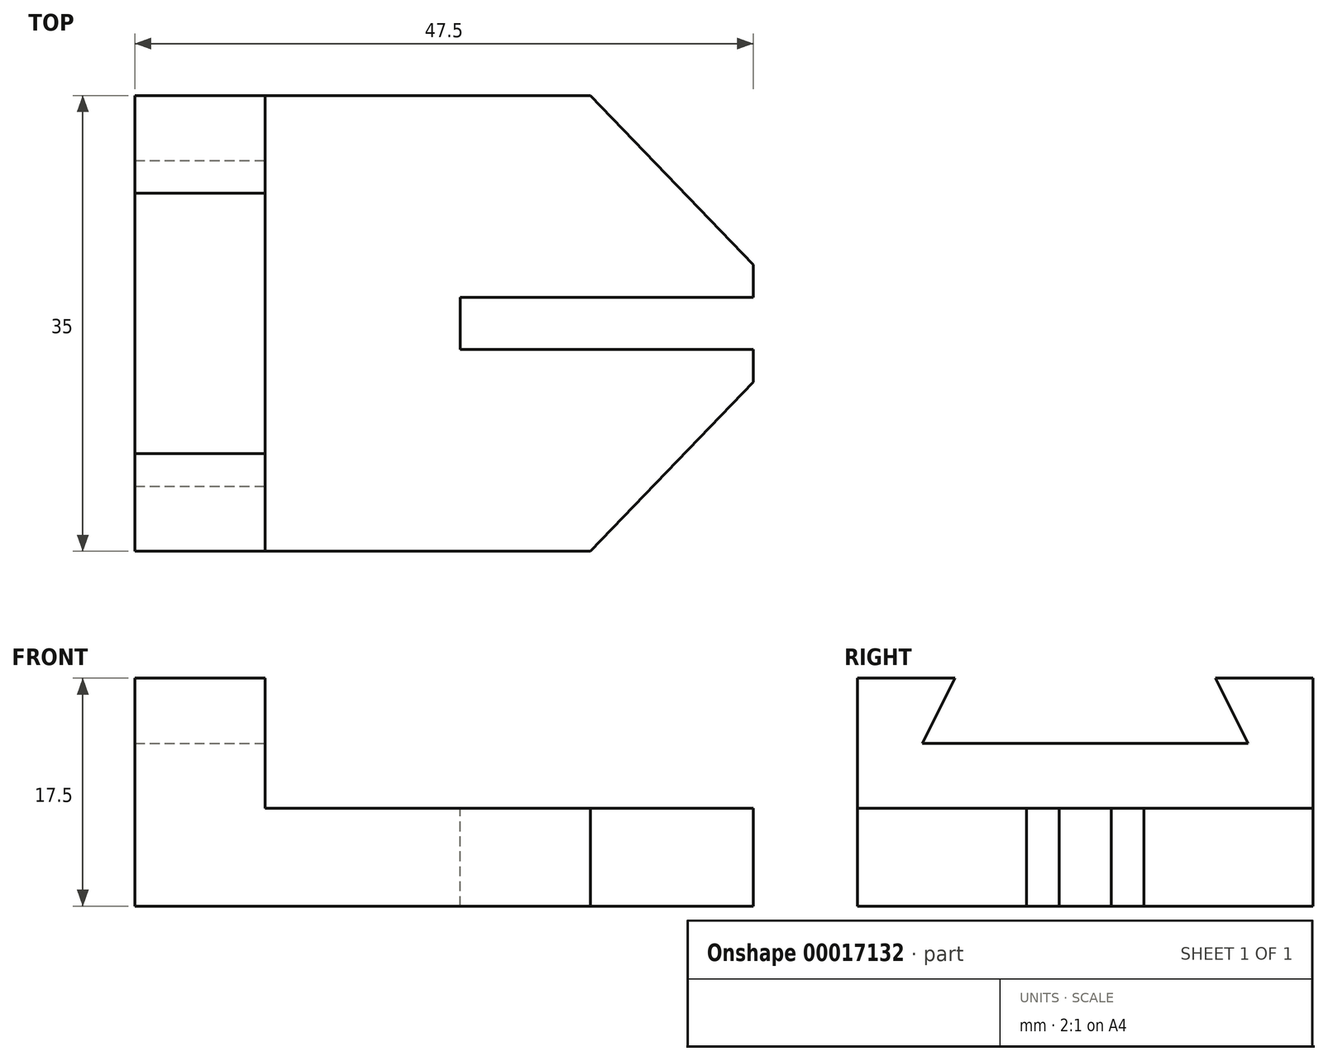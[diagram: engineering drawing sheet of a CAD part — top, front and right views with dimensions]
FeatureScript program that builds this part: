
annotation { "Feature Type Name" : "Feature", "Feature Type Description" : "" }
export const myFeature = defineFeature(function(context is Context, id is Id, definition is map)
    precondition{}
    {
        {
            var Q0;
            Q0=qCreatedBy(makeId("Front.planeOp"),FACE);
            var sketch = newSketch(context, id + "F0", { "sketchPlane" : qUnion([Q0])});
            skLineSegment(sketch, "E0.bottom", {"start": v(-18.49, -11.72) * mm, "end": v(29.01, -11.72) * mm});
            skLineSegment(sketch, "E0.top", {"start": v(-18.49, -19.22) * mm, "end": v(29.01, -19.22) * mm});
            skLineSegment(sketch, "E0.left", {"start": v(-18.49, -11.72) * mm, "end": v(-18.49, -19.22) * mm});
            skLineSegment(sketch, "E0.right", {"start": v(29.01, -11.72) * mm, "end": v(29.01, -19.22) * mm});
            skSolve(sketch);
        }
        {
            var Q0;
            Q0=makeQuery(id+"F0.imprint","IMPRINT",FACE,{"disambiguationData":[TD([[makeQuery(id+"F0.imprint","IMPRINT",EDGE,{"derivedFrom":sQuery(id+"F0.wireOp",EDGE,"E0.bottom")}),-1.0]])]});
            extrude(context, id + "F1", {"entities" : qUnion([Q0]), "depth" : 35 * mm});
        }
        {
            var Q0;
            Q0=makeQuery(id+"F1.opExtrude","SWEPT_FACE",FACE,{"disambiguationData":[OSD([sQuery(id+"F0.wireOp",EDGE,"E0.bottom")])]});
            var sketch = newSketch(context, id + "F2", { "sketchPlane" : qUnion([Q0])});
            skLineSegment(sketch, "E1", {"start": v(-8.49, 0) * mm, "end": v(-8.49, -35) * mm});
            skLineSegment(sketch, "E2", {"start": v(-18.49, 0) * mm, "end": v(-8.49, 0) * mm});
            skSolve(sketch);
        }
        {
            var Q0;
            {var subQ2=sQuery(id+"F2.wireOp",EDGE,"E1");Q0=makeQuery(id+"F2.imprint","IMPRINT",FACE,{"disambiguationData":[TD([[makeQuery(id+"F2.imprint","IMPRINT",EDGE,{"derivedFrom":subQ2}),-1.0]])]});}
            extrude(context, id + "F3", {"entities" : qUnion([Q0]), "operationType" : NewBodyOperationType.ADD, "depth" : 10 * mm});
        }
        {
            var Q0;
            Q0=makeQuery(id+"F1.opExtrude","SWEPT_FACE",FACE,{"disambiguationData":[OSD([sQuery(id+"F0.wireOp",EDGE,"E0.bottom")])]});
            var sketch = newSketch(context, id + "F4", { "sketchPlane" : qUnion([Q0])});
            skLineSegment(sketch, "E3.bottom", {"start": v(29.01, -15.5) * mm, "end": v(6.51, -15.5) * mm});
            skLineSegment(sketch, "E3.top", {"start": v(29.01, -19.5) * mm, "end": v(6.51, -19.5) * mm});
            skLineSegment(sketch, "E3.left", {"start": v(29.01, -15.5) * mm, "end": v(29.01, -19.5) * mm});
            skLineSegment(sketch, "E3.right", {"start": v(6.51, -15.5) * mm, "end": v(6.51, -19.5) * mm});
            skLineSegment(sketch, "E4", {"start": v(29.01, -19.5) * mm, "end": v(29.01, -35) * mm});
            skLineSegment(sketch, "E5", {"start": v(29.01, -15.5) * mm, "end": v(29.01, 0) * mm});
            skSolve(sketch);
        }
        {
            var Q0;
            Q0=makeQuery(id+"F4.imprint","IMPRINT",FACE,{"disambiguationData":[TD([[makeQuery(id+"F4.imprint","IMPRINT",EDGE,{"derivedFrom":sQuery(id+"F4.wireOp",EDGE,"E3.bottom")}),1.0]])]});
            extrude(context, id + "F5", {"entities" : qUnion([Q0]), "operationType" : NewBodyOperationType.REMOVE, "endBound" : BoundingType.THROUGH_ALL, "oppositeDirection" : true, "depth" : 25 * mm});
        }
        {
            var Q0;
            Q0=makeQuery(id+"F1.opExtrude","SWEPT_FACE",FACE,{"disambiguationData":[OSD([sQuery(id+"F0.wireOp",EDGE,"E0.bottom")])]});
            var sketch = newSketch(context, id + "F6", { "sketchPlane" : qUnion([Q0])});
            skLineSegment(sketch, "E6", {"start": v(16.51, -35) * mm, "end": v(29.01, -22) * mm});
            skLineSegment(sketch, "E7", {"start": v(16.51, 0) * mm, "end": v(29.01, -13) * mm});
            skLineSegment(sketch, "E8", {"start": v(16.51, -35) * mm, "end": v(29.01, -35) * mm});
            skLineSegment(sketch, "E9", {"start": v(29.01, -35) * mm, "end": v(29.01, -22) * mm});
            skLineSegment(sketch, "E10", {"start": v(29.01, -13) * mm, "end": v(29.01, 0) * mm});
            skLineSegment(sketch, "E11", {"start": v(29.01, 0) * mm, "end": v(16.51, 0) * mm});
            skSolve(sketch);
        }
        {
            var Q0;
            Q0=makeQuery(id+"F6.imprint","IMPRINT",FACE,{"disambiguationData":[TD([[makeQuery(id+"F6.imprint","IMPRINT",EDGE,{"derivedFrom":sQuery(id+"F6.wireOp",EDGE,"E6")}),-1.0]])]});
            var Q1;
            Q1=makeQuery(id+"F6.imprint","IMPRINT",FACE,{"disambiguationData":[TD([[makeQuery(id+"F6.imprint","IMPRINT",EDGE,{"derivedFrom":sQuery(id+"F6.wireOp",EDGE,"E7")}),1.0]])]});
            extrude(context, id + "F7", {"entities" : qUnion([Q0, Q1]), "operationType" : NewBodyOperationType.REMOVE, "endBound" : BoundingType.THROUGH_ALL, "oppositeDirection" : true, "depth" : 25 * mm});
        }
        {
            var Q0;
            Q0=makeQuery(id+"F3.opExtrude","SWEPT_FACE",FACE,{"disambiguationData":[OSD([sQuery(id+"F2.wireOp",EDGE,"E1")])]});
            var sketch = newSketch(context, id + "F8", { "sketchPlane" : qUnion([Q0])});
            skLineSegment(sketch, "E12", {"start": v(-30, -6.72) * mm, "end": v(-5, -6.72) * mm});
            skLineSegment(sketch, "E13", {"start": v(-5, -6.72) * mm, "end": v(-7.5, -1.72) * mm});
            skLineSegment(sketch, "E14", {"start": v(-30, -6.72) * mm, "end": v(-27.5, -1.72) * mm});
            skLineSegment(sketch, "E15", {"start": v(-27.5, -1.72) * mm, "end": v(-7.5, -1.72) * mm});
            skSolve(sketch);
        }
        {
            var Q0;
            Q0=makeQuery(id+"F8.imprint","IMPRINT",FACE,{"disambiguationData":[TD([[makeQuery(id+"F8.imprint","IMPRINT",EDGE,{"derivedFrom":sQuery(id+"F8.wireOp",EDGE,"E12")}),1.0]])]});
            extrude(context, id + "F9", {"entities" : qUnion([Q0]), "operationType" : NewBodyOperationType.REMOVE, "endBound" : BoundingType.THROUGH_ALL, "oppositeDirection" : true, "depth" : 25 * mm});
        }
    });
